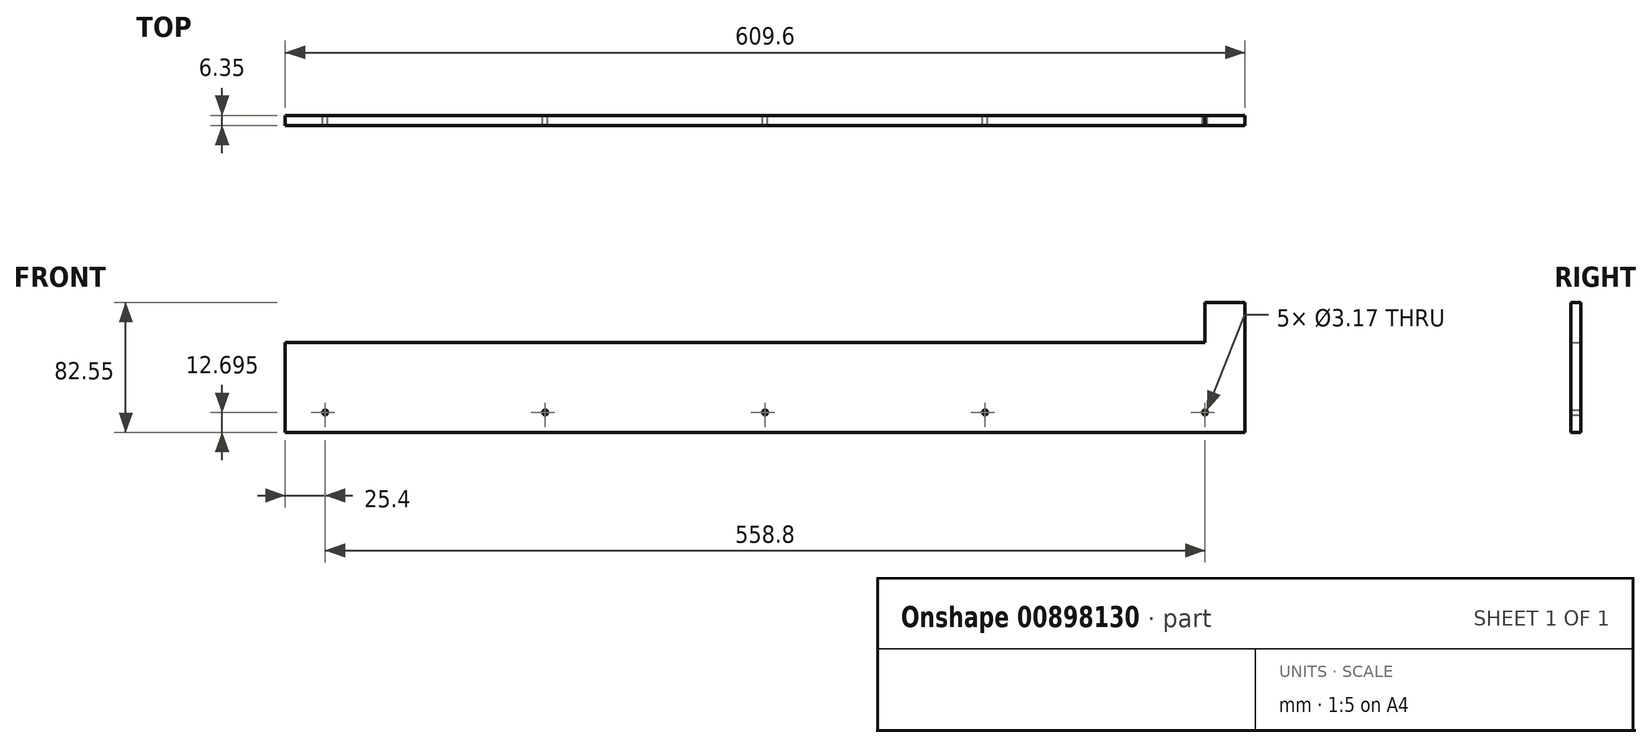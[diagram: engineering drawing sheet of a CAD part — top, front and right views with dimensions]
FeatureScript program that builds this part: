
annotation { "Feature Type Name" : "Feature", "Feature Type Description" : "" }
export const myFeature = defineFeature(function(context is Context, id is Id, definition is map)
    precondition{}
    {
        {
            var Q0;
            Q0=qCreatedBy(makeId("Front.planeOp"),FACE);
            var sketch = newSketch(context, id + "F0", { "sketchPlane" : qUnion([Q0])});
            skLineSegment(sketch, "E0.bottom", {"start": v(304.8, -28.57) * mm, "end": v(-304.8, -28.58) * mm});
            skLineSegment(sketch, "E0.top", {"start": v(279.4, 28.58) * mm, "end": v(-304.8, 28.57) * mm});
            skLineSegment(sketch, "E0.left", {"start": v(304.8, -28.57) * mm, "end": v(304.8, 28.58) * mm});
            skLineSegment(sketch, "E0.right", {"start": v(-304.8, -28.58) * mm, "end": v(-304.8, 28.57) * mm});
            skPoint(sketch, "E0.middle", {"position": v(0, 0) * mm});
            skLineSegment(sketch, "E1.top", {"start": v(304.8, 53.98) * mm, "end": v(279.4, 53.98) * mm});
            skLineSegment(sketch, "E1.left", {"start": v(304.8, 28.58) * mm, "end": v(304.8, 53.98) * mm});
            skLineSegment(sketch, "E1.right", {"start": v(279.4, 28.58) * mm, "end": v(279.4, 53.98) * mm});
            skLineSegment(sketch, "E2", {"start": v(-304.8, -15.88) * mm, "end": v(304.8, -15.88) * mm, "construction": true});
            skCircle(sketch, "E3", {"center": v(0, -15.88) * mm, "radius": 1.59 * mm});
            skCircle(sketch, "E4.1.0.0", {"center": v(139.7, -15.88) * mm, "radius": 1.59 * mm});
            skLineSegment(sketch, "E4.direction1", {"start": v(0, -15.88) * mm, "end": v(139.7, -15.88) * mm, "construction": true});
            skCircle(sketch, "E5.0.2.0", {"center": v(279.4, -15.88) * mm, "radius": 1.59 * mm});
            skCircle(sketch, "E6.1.0.0", {"center": v(-139.7, -15.88) * mm, "radius": 1.59 * mm});
            skCircle(sketch, "E6.2.0.0", {"center": v(-279.4, -15.88) * mm, "radius": 1.59 * mm});
            skLineSegment(sketch, "E6.direction1", {"start": v(0, -15.88) * mm, "end": v(-139.7, -15.88) * mm, "construction": true});
            skSolve(sketch);
        }
        {
            var Q0;
            Q0=makeQuery(id+"F0.imprint","IMPRINT",FACE,{"disambiguationData":[TD([[makeQuery(id+"F0.imprint","IMPRINT",EDGE,{"derivedFrom":sQuery(id+"F0.wireOp",EDGE,"E0.bottom")}),-1.0]])]});
            extrude(context, id + "F1", {"entities" : qUnion([Q0]), "depth" : 6.35 * mm, "offsetDistance" : 25.4 * mm});
        }
    });
